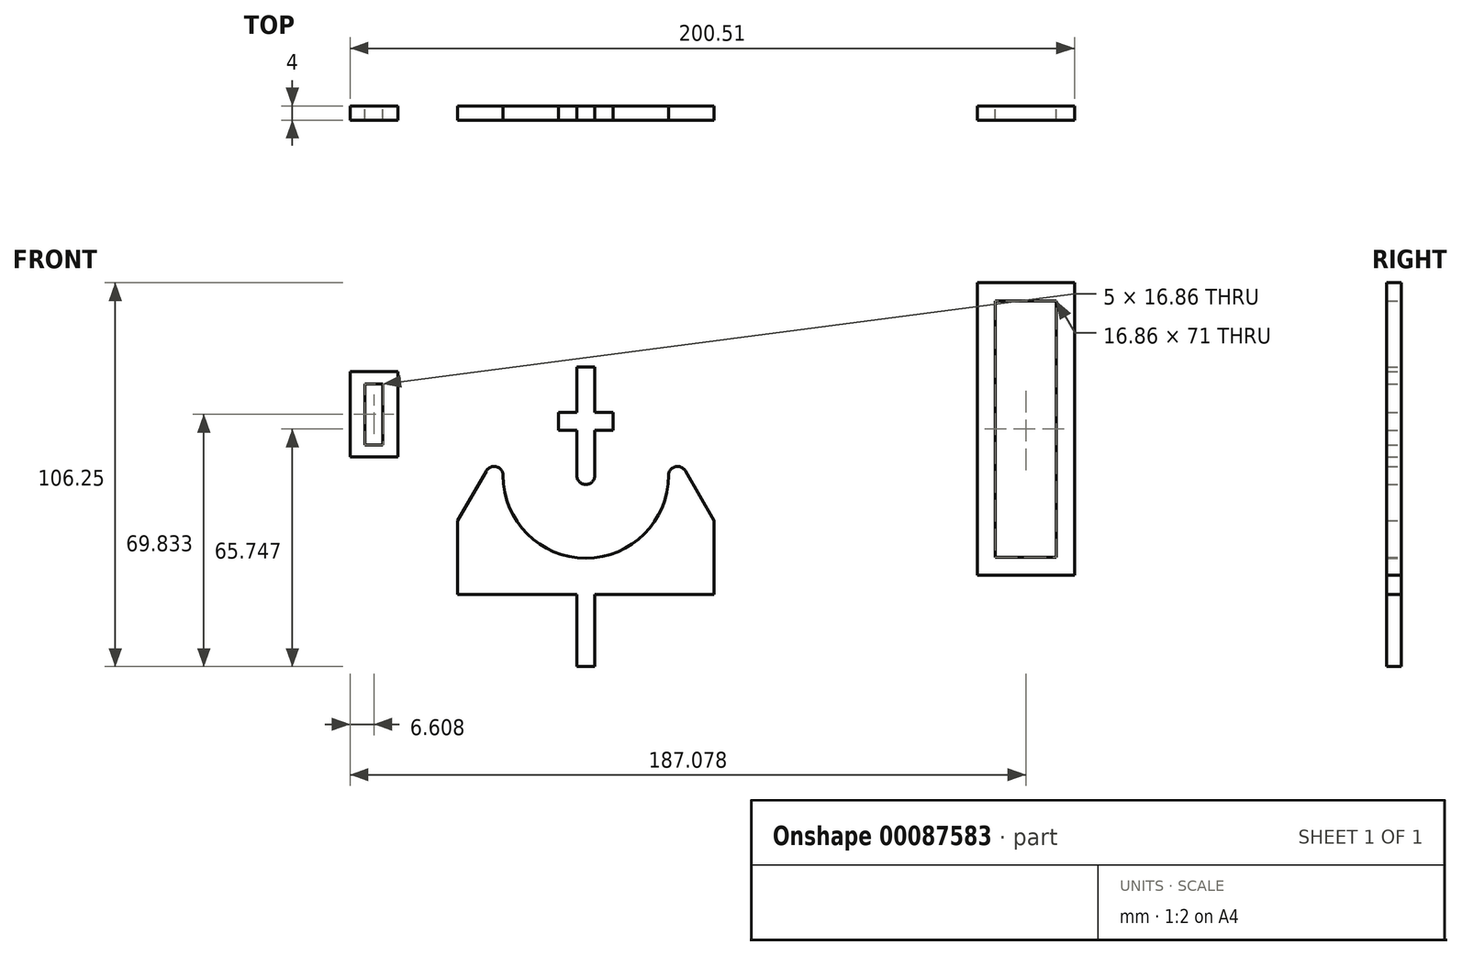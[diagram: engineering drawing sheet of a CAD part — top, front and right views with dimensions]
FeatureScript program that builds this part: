
annotation { "Feature Type Name" : "Feature", "Feature Type Description" : "" }
export const myFeature = defineFeature(function(context is Context, id is Id, definition is map)
    precondition{}
    {
        {
            var Q0;
            Q0=qCreatedBy(makeId("Front.planeOp"),FACE);
            var sketch = newSketch(context, id + "F0", { "sketchPlane" : qUnion([Q0])});
            skArc(sketch, "E0", {"start": v(-22.9, 0) * mm, "mid": v(-24.75, 2.41) * mm, "end": v(-27.57, 1.25) * mm});
            skArc(sketch, "E1", {"start": v(-22.9, 0) * mm, "mid": v(-16.2, -16.2) * mm, "end": v(0, -22.9) * mm});
            skLineSegment(sketch, "E2", {"start": v(-35.5, -32.9) * mm, "end": v(-2.5, -32.9) * mm});
            skLineSegment(sketch, "E3", {"start": v(0, -32.9) * mm, "end": v(0, -22.9) * mm, "construction": true});
            skLineSegment(sketch, "E4", {"start": v(-27.57, 1.25) * mm, "end": v(-35.5, -12.5) * mm});
            skArc(sketch, "E5.MirrorCS", {"start": v(22.9, 0) * mm, "mid": v(24.75, 2.41) * mm, "end": v(27.57, 1.25) * mm});
            skLineSegment(sketch, "E6.MirrorCS", {"start": v(27.57, 1.25) * mm, "end": v(35.5, -12.5) * mm});
            skArc(sketch, "E7.MirrorCS", {"start": v(22.9, 0) * mm, "mid": v(16.2, -16.2) * mm, "end": v(0, -22.9) * mm});
            skLineSegment(sketch, "E8.MirrorCS", {"start": v(35.5, -32.9) * mm, "end": v(2.5, -32.9) * mm});
            skArc(sketch, "E9", {"start": v(-2.5, 0) * mm, "mid": v(0, -2.5) * mm, "end": v(2.5, 0) * mm});
            skLineSegment(sketch, "E10", {"start": v(2.5, 0) * mm, "end": v(2.5, 12.5) * mm});
            skLineSegment(sketch, "E11", {"start": v(-2.5, 0) * mm, "end": v(-2.5, 12.5) * mm});
            skLineSegment(sketch, "E12", {"start": v(-2.5, 30) * mm, "end": v(2.5, 30) * mm});
            skLineSegment(sketch, "E13.bottom", {"start": v(-7.5, 12.5) * mm, "end": v(-2.5, 12.5) * mm});
            skLineSegment(sketch, "E13.top", {"start": v(-7.5, 17.5) * mm, "end": v(-2.5, 17.5) * mm});
            skLineSegment(sketch, "E13.left", {"start": v(-7.5, 12.5) * mm, "end": v(-7.5, 17.5) * mm});
            skLineSegment(sketch, "E13.right", {"start": v(7.5, 12.5) * mm, "end": v(7.5, 17.5) * mm});
            skPoint(sketch, "E13.middle", {"position": v(0, 15) * mm});
            skLineSegment(sketch, "E14.trimOffspring", {"start": v(2.5, 17.5) * mm, "end": v(7.5, 17.5) * mm});
            skLineSegment(sketch, "E15.trimOffspring", {"start": v(2.5, 17.5) * mm, "end": v(2.5, 30) * mm});
            skLineSegment(sketch, "E16.trimOffspring", {"start": v(-2.5, 17.5) * mm, "end": v(-2.5, 30) * mm});
            skLineSegment(sketch, "E17.trimOffspring", {"start": v(2.5, 12.5) * mm, "end": v(7.5, 12.5) * mm});
            skLineSegment(sketch, "E18.top", {"start": v(2.5, -52.9) * mm, "end": v(-2.5, -52.9) * mm});
            skLineSegment(sketch, "E18.left", {"start": v(2.5, -32.9) * mm, "end": v(2.5, -52.9) * mm});
            skLineSegment(sketch, "E18.right", {"start": v(-2.5, -32.9) * mm, "end": v(-2.5, -52.9) * mm});
            skPoint(sketch, "E18.middle", {"position": v(0, -42.9) * mm});
            skPoint(sketch, "E19.orphan", {"position": v(0, -32.9) * mm});
            skLineSegment(sketch, "E20", {"start": v(-35.5, -12.5) * mm, "end": v(-35.5, -32.9) * mm});
            skLineSegment(sketch, "E21", {"start": v(35.5, -12.5) * mm, "end": v(35.5, -32.9) * mm});
            skPoint(sketch, "E22.orphan", {"position": v(-47.28, -32.9) * mm});
            skPoint(sketch, "E23.orphan", {"position": v(47.28, -32.9) * mm});
            skSolve(sketch);
        }
        {
            var Q0;
            Q0 = qSketchRegion(id + "F0", true);
            extrude(context, id + "F1", {"entities" : qUnion([Q0]), "depth" : 4 * mm});
        }
        {
            var Q0;
            Q0=qCreatedBy(makeId("Front.planeOp"),FACE);
            var sketch = newSketch(context, id + "F2", { "sketchPlane" : qUnion([Q0])});
            skLineSegment(sketch, "E24.bottom", {"start": v(-52.04, 5.15) * mm, "end": v(-65.25, 5.15) * mm});
            skLineSegment(sketch, "E24.top", {"start": v(-52.04, 28.72) * mm, "end": v(-65.25, 28.72) * mm});
            skLineSegment(sketch, "E24.left", {"start": v(-52.04, 5.15) * mm, "end": v(-52.04, 28.72) * mm});
            skLineSegment(sketch, "E24.right", {"start": v(-65.25, 5.15) * mm, "end": v(-65.25, 28.72) * mm});
            skPoint(sketch, "E24.middle", {"position": v(-58.64, 16.93) * mm});
            skLineSegment(sketch, "E25.bottom", {"start": v(-56.14, 8.5) * mm, "end": v(-61.14, 8.5) * mm});
            skLineSegment(sketch, "E25.top", {"start": v(-56.14, 25.36) * mm, "end": v(-61.14, 25.36) * mm});
            skLineSegment(sketch, "E25.left", {"start": v(-56.14, 8.5) * mm, "end": v(-56.14, 25.36) * mm});
            skLineSegment(sketch, "E25.right", {"start": v(-61.14, 8.5) * mm, "end": v(-61.14, 25.36) * mm});
            skLineSegment(sketch, "E26.bottom", {"start": v(135.26, 53.35) * mm, "end": v(108.4, 53.35) * mm});
            skLineSegment(sketch, "E26.top", {"start": v(135.26, -27.65) * mm, "end": v(108.4, -27.65) * mm});
            skLineSegment(sketch, "E26.left", {"start": v(135.26, 53.35) * mm, "end": v(135.26, -27.65) * mm});
            skLineSegment(sketch, "E26.right", {"start": v(108.4, 53.35) * mm, "end": v(108.4, -27.65) * mm});
            skPoint(sketch, "E26.middle", {"position": v(121.83, 12.85) * mm});
            skLineSegment(sketch, "E27.bottom", {"start": v(130.26, 48.35) * mm, "end": v(113.4, 48.35) * mm});
            skLineSegment(sketch, "E27.top", {"start": v(130.26, -22.65) * mm, "end": v(113.4, -22.65) * mm});
            skLineSegment(sketch, "E27.left", {"start": v(130.26, 48.35) * mm, "end": v(130.26, -22.65) * mm});
            skLineSegment(sketch, "E27.right", {"start": v(113.4, 48.35) * mm, "end": v(113.4, -22.65) * mm});
            skSolve(sketch);
        }
        {
            var Q0;
            Q0=makeQuery(id+"F2.imprint","IMPRINT",FACE,{"disambiguationData":[TD([[makeQuery(id+"F2.imprint","IMPRINT",EDGE,{"derivedFrom":sQuery(id+"F2.wireOp",EDGE,"E24.bottom")}),-1.0]])]});
            var Q1;
            Q1=makeQuery(id+"F2.imprint","IMPRINT",FACE,{"disambiguationData":[TD([[makeQuery(id+"F2.imprint","IMPRINT",EDGE,{"derivedFrom":sQuery(id+"F2.wireOp",EDGE,"E26.bottom")}),1.0]])]});
            extrude(context, id + "F3", {"entities" : qUnion([Q0, Q1]), "depth" : 4 * mm});
        }
    });
